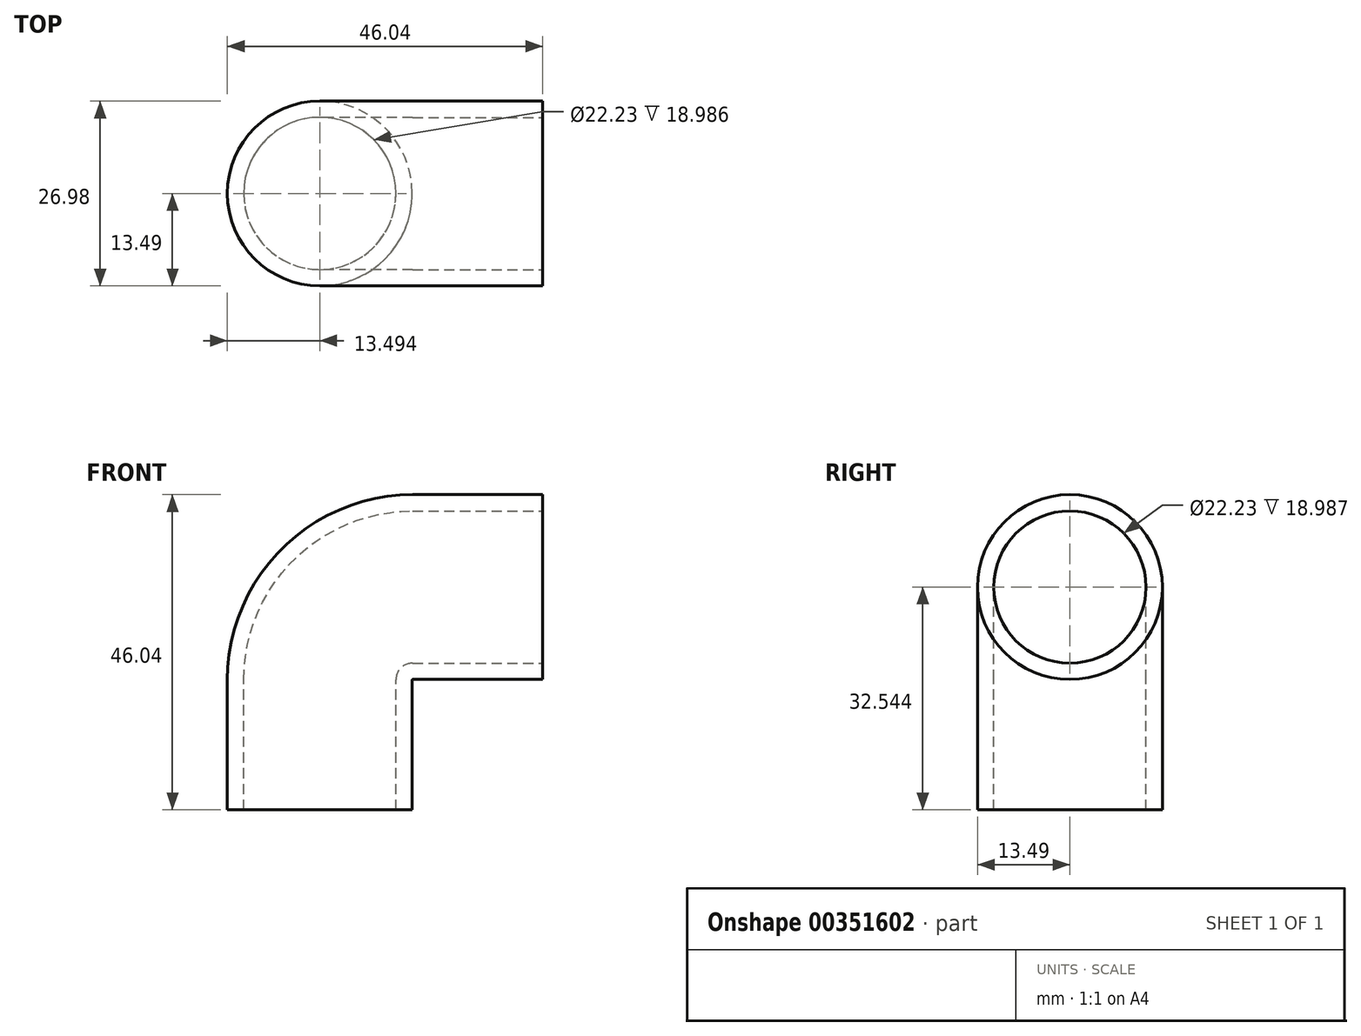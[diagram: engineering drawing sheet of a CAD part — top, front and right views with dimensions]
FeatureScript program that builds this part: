
annotation { "Feature Type Name" : "Feature", "Feature Type Description" : "" }
export const myFeature = defineFeature(function(context is Context, id is Id, definition is map)
    precondition{}
    {
        {
            var Q0;
            Q0=qCreatedBy(makeId("Front.planeOp"),FACE);
            var sketch = newSketch(context, id + "F0", { "sketchPlane" : qUnion([Q0])});
            skLineSegment(sketch, "E0", {"start": v(0, 0) * mm, "end": v(0, 46.04) * mm, "construction": true});
            skLineSegment(sketch, "E1", {"start": v(0, 46.04) * mm, "end": v(46.04, 46.04) * mm, "construction": true});
            skArc(sketch, "E2", {"start": v(27.05, 46.04) * mm, "mid": v(7.92, 38.11) * mm, "end": v(0, 18.99) * mm});
            skLineSegment(sketch, "E3", {"start": v(0, 18.99) * mm, "end": v(0, 0) * mm});
            skLineSegment(sketch, "E4", {"start": v(27.05, 46.04) * mm, "end": v(46.04, 46.04) * mm});
            skSolve(sketch);
        }
        {
            var Q0;
            Q0=qCreatedBy(makeId("Top.planeOp"),FACE);
            var sketch = newSketch(context, id + "F1", { "sketchPlane" : qUnion([Q0])});
            skCircle(sketch, "E5", {"center": v(13.5, 0) * mm, "radius": 13.5 * mm});
            skLineSegment(sketch, "E6", {"start": v(0, 24.93) * mm, "end": v(0, -33.13) * mm, "construction": true});
            skSolve(sketch);
        }
        {
            var Q0;
            Q0 = qSketchRegion(id + "F1", true);
            var Q1;
            Q1 = qConstructionFilter(qBodyType(qCreatedBy(id + "F0" ,EDGE), BodyType.WIRE), ConstructionObject.NO);
            sweep(context, id + "F2", {"profiles" : qUnion([Q0]), "path" : qUnion([Q1])});
        }
        {
            var Q0;
            Q0=makeQuery(id+"F2.opSweep","CAP_FACE",FACE,{"disambiguationData":[OSD([sQuery(id+"F0.wireOp",VERTEX,"E3.end"),sQuery(id+"F1.wireOp",EDGE,"E5")])],"isStart":true});
            var sketch = newSketch(context, id + "F3", { "sketchPlane" : qUnion([Q0])});
            skCircle(sketch, "E7", {"center": v(13.5, 0) * mm, "radius": 11.11 * mm});
            skSolve(sketch);
        }
        {
            var Q0;
            Q0 = qSketchRegion(id + "F3", true);
            var Q1;
            Q1 = qConstructionFilter(qBodyType(qCreatedBy(id + "F0" ,EDGE), BodyType.WIRE), ConstructionObject.NO);
            sweep(context, id + "F4", {"operationType" : NewBodyOperationType.REMOVE, "profiles" : qUnion([Q0]), "path" : qUnion([Q1])});
        }
    });
